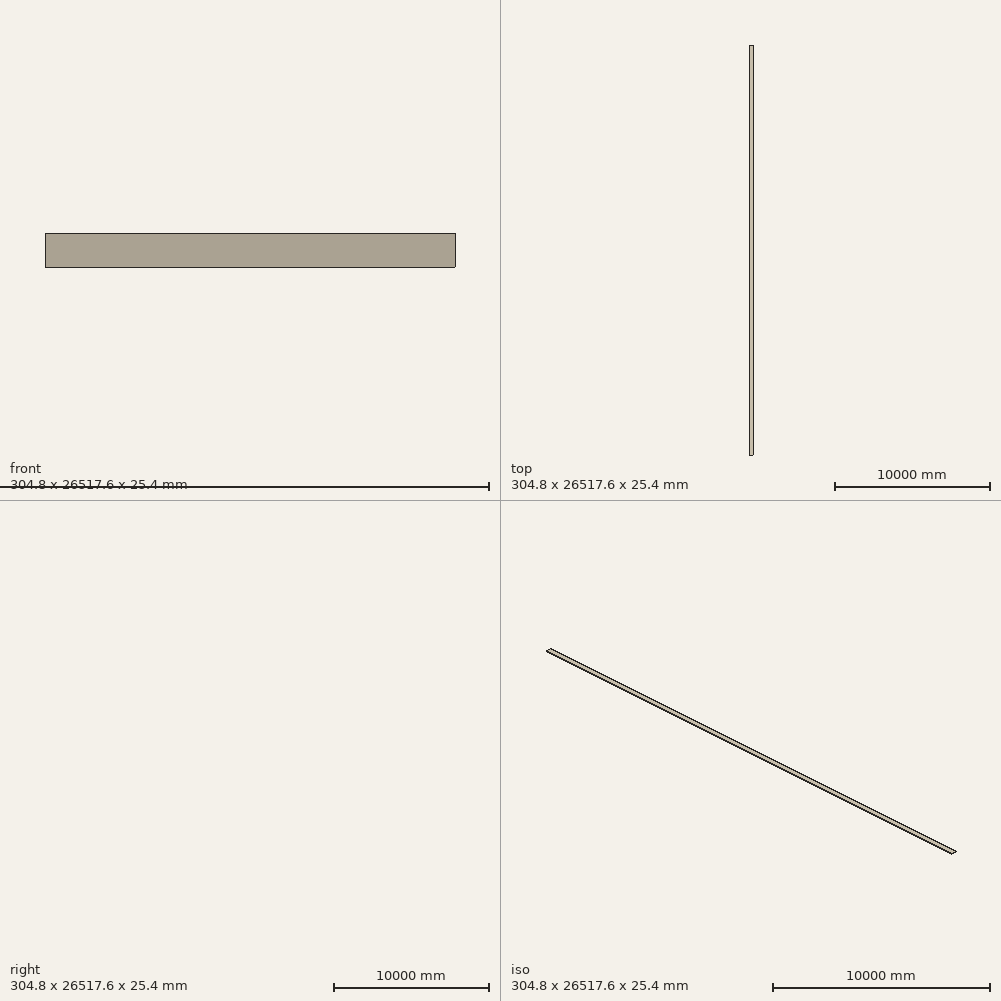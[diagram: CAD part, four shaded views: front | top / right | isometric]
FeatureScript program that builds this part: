
annotation { "Feature Type Name" : "Feature", "Feature Type Description" : "" }
export const myFeature = defineFeature(function(context is Context, id is Id, definition is map)
    precondition{}
    {
        {
            var Q0;
            Q0=qCreatedBy(makeId("Top.planeOp"),FACE);
            var sketch = newSketch(context, id + "F0", { "sketchPlane" : qUnion([Q0])});
            skLineSegment(sketch, "E0.bottom", {"start": v(152.4, 13258.8) * mm, "end": v(-152.4, 13258.8) * mm});
            skLineSegment(sketch, "E0.top", {"start": v(152.4, -13258.8) * mm, "end": v(-152.4, -13258.8) * mm});
            skLineSegment(sketch, "E0.left", {"start": v(152.4, 13258.8) * mm, "end": v(152.4, -13258.8) * mm});
            skLineSegment(sketch, "E0.right", {"start": v(-152.4, 13258.8) * mm, "end": v(-152.4, -13258.8) * mm});
            skPoint(sketch, "E0.middle", {"position": v(0, 0) * mm});
            skSolve(sketch);
        }
        {
            var Q0;
            Q0 = qSketchRegion(id + "F0", true);
            extrude(context, id + "F1", {"entities" : qUnion([Q0]), "depth" : 25.4 * mm, "offsetDistance" : 25.4 * mm});
        }
    });
